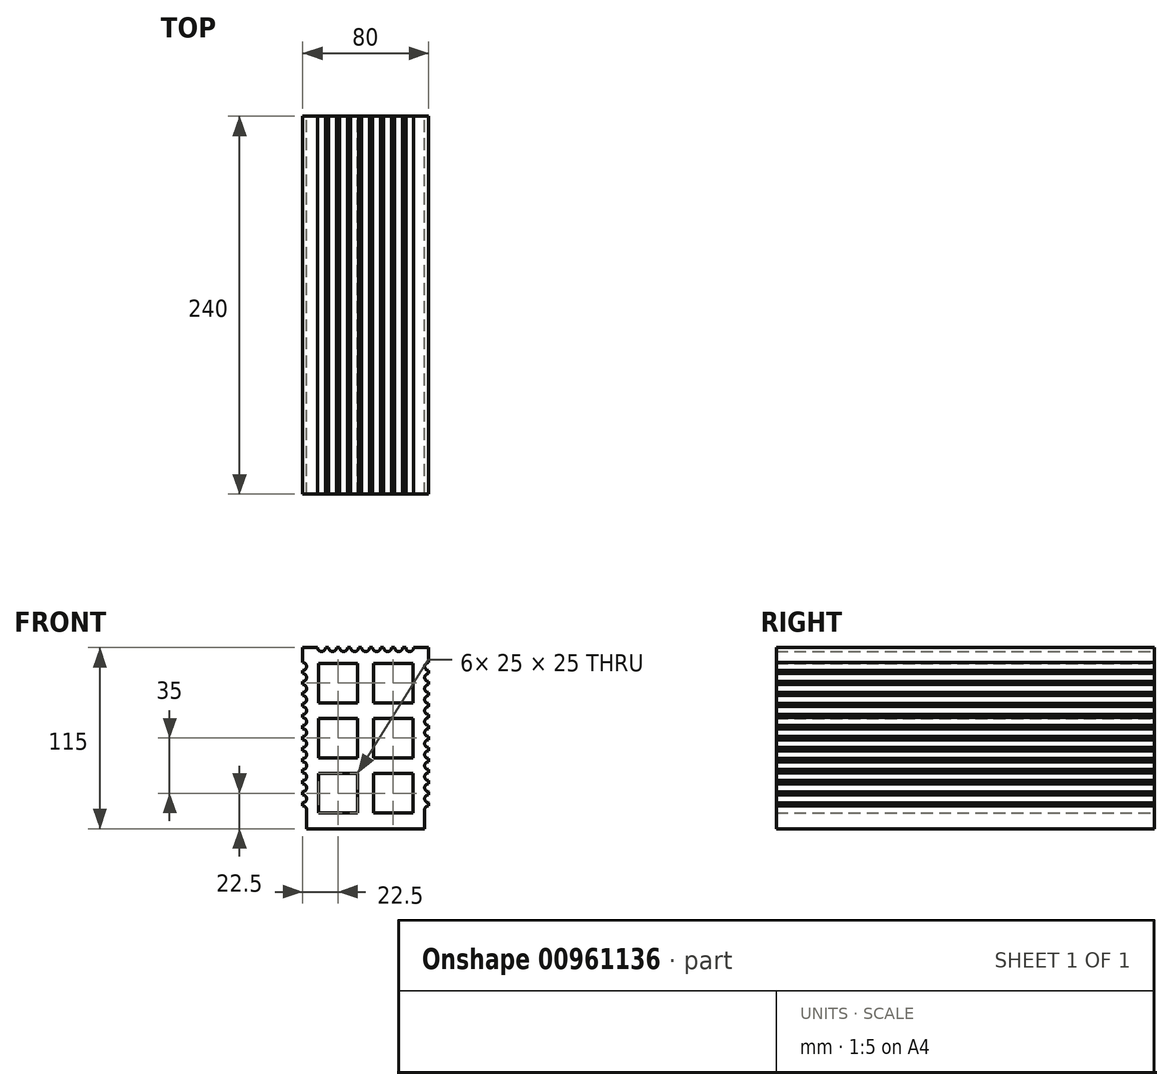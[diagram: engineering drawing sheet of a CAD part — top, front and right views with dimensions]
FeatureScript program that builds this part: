
annotation { "Feature Type Name" : "Feature", "Feature Type Description" : "" }
export const myFeature = defineFeature(function(context is Context, id is Id, definition is map)
    precondition{}
    {
        {
            var Q0;
            Q0=qCreatedBy(makeId("Front.planeOp"),FACE);
            var sketch = newSketch(context, id + "F0", { "sketchPlane" : qUnion([Q0])});
            skLineSegment(sketch, "E0.bottom", {"start": v(-40, -57.5) * mm, "end": v(40, -57.5) * mm});
            skLineSegment(sketch, "E0.top", {"start": v(-40, 57.5) * mm, "end": v(40, 57.5) * mm});
            skLineSegment(sketch, "E0.left", {"start": v(-40, -57.5) * mm, "end": v(-40, 57.5) * mm});
            skLineSegment(sketch, "E0.right", {"start": v(40, -57.5) * mm, "end": v(40, 57.5) * mm});
            skLineSegment(sketch, "E1.bottom", {"start": v(-30, 47.5) * mm, "end": v(-5, 47.5) * mm});
            skLineSegment(sketch, "E1.top", {"start": v(-30, 22.5) * mm, "end": v(-5, 22.5) * mm});
            skLineSegment(sketch, "E1.left", {"start": v(-30, 47.5) * mm, "end": v(-30, 22.5) * mm});
            skLineSegment(sketch, "E1.right", {"start": v(-5, 47.5) * mm, "end": v(-5, 22.5) * mm});
            skLineSegment(sketch, "E2.0.1.0", {"start": v(-30, 12.5) * mm, "end": v(-30, -12.5) * mm});
            skLineSegment(sketch, "E2.0.1.1", {"start": v(-30, 12.5) * mm, "end": v(-5, 12.5) * mm});
            skLineSegment(sketch, "E2.0.1.2", {"start": v(-5, 12.5) * mm, "end": v(-5, -12.5) * mm});
            skLineSegment(sketch, "E2.0.1.3", {"start": v(-30, -12.5) * mm, "end": v(-5, -12.5) * mm});
            skLineSegment(sketch, "E2.0.2.0", {"start": v(-30, -22.5) * mm, "end": v(-30, -47.5) * mm});
            skLineSegment(sketch, "E2.0.2.1", {"start": v(-30, -22.5) * mm, "end": v(-5, -22.5) * mm});
            skLineSegment(sketch, "E2.0.2.2", {"start": v(-5, -22.5) * mm, "end": v(-5, -47.5) * mm});
            skLineSegment(sketch, "E2.0.2.3", {"start": v(-30, -47.5) * mm, "end": v(-5, -47.5) * mm});
            skLineSegment(sketch, "E2.1.0.0", {"start": v(5, 47.5) * mm, "end": v(5, 22.5) * mm});
            skLineSegment(sketch, "E2.1.0.1", {"start": v(5, 47.5) * mm, "end": v(30, 47.5) * mm});
            skLineSegment(sketch, "E2.1.0.2", {"start": v(30, 47.5) * mm, "end": v(30, 22.5) * mm});
            skLineSegment(sketch, "E2.1.0.3", {"start": v(5, 22.5) * mm, "end": v(30, 22.5) * mm});
            skLineSegment(sketch, "E2.1.1.0", {"start": v(5, 12.5) * mm, "end": v(5, -12.5) * mm});
            skLineSegment(sketch, "E2.1.1.1", {"start": v(5, 12.5) * mm, "end": v(30, 12.5) * mm});
            skLineSegment(sketch, "E2.1.1.2", {"start": v(30, 12.5) * mm, "end": v(30, -12.5) * mm});
            skLineSegment(sketch, "E2.1.1.3", {"start": v(5, -12.5) * mm, "end": v(30, -12.5) * mm});
            skLineSegment(sketch, "E2.1.2.0", {"start": v(5, -22.5) * mm, "end": v(5, -47.5) * mm});
            skLineSegment(sketch, "E2.1.2.1", {"start": v(5, -22.5) * mm, "end": v(30, -22.5) * mm});
            skLineSegment(sketch, "E2.1.2.2", {"start": v(30, -22.5) * mm, "end": v(30, -47.5) * mm});
            skLineSegment(sketch, "E2.1.2.3", {"start": v(5, -47.5) * mm, "end": v(30, -47.5) * mm});
            skLineSegment(sketch, "E2.direction1", {"start": v(-30, 22.5) * mm, "end": v(5, 22.5) * mm, "construction": true});
            skLineSegment(sketch, "E2.direction2", {"start": v(-30, 22.5) * mm, "end": v(-30, -12.5) * mm, "construction": true});
            skLineSegment(sketch, "E3", {"start": v(-40, 57.5) * mm, "end": v(-40, 48) * mm});
            skLineSegment(sketch, "E4", {"start": v(-40, 48) * mm, "end": v(-40, 43) * mm});
            skLineSegment(sketch, "E5", {"start": v(-40, 43) * mm, "end": v(-40, 41) * mm});
            skLineSegment(sketch, "E6", {"start": v(-37.5, -45.5) * mm, "end": v(-37.5, -57.5) * mm});
            skLineSegment(sketch, "E7", {"start": v(-40, 57.5) * mm, "end": v(-30.5, 57.5) * mm});
            skLineSegment(sketch, "E8", {"start": v(-30.5, 57.5) * mm, "end": v(-25.5, 57.5) * mm});
            skLineSegment(sketch, "E9", {"start": v(-25.5, 57.5) * mm, "end": v(-23.5, 57.5) * mm});
            skArc(sketch, "E10", {"start": v(-30.5, 57.5) * mm, "mid": v(-28, 55) * mm, "end": v(-25.5, 57.5) * mm});
            skArc(sketch, "E11.1.0.0", {"start": v(-23.5, 57.5) * mm, "mid": v(-21, 55) * mm, "end": v(-18.5, 57.5) * mm});
            skLineSegment(sketch, "E11.1.0.1", {"start": v(-18.5, 57.5) * mm, "end": v(-16.5, 57.5) * mm});
            skArc(sketch, "E11.2.0.0", {"start": v(-16.5, 57.5) * mm, "mid": v(-14, 55) * mm, "end": v(-11.5, 57.5) * mm});
            skLineSegment(sketch, "E11.2.0.1", {"start": v(-11.5, 57.5) * mm, "end": v(-9.5, 57.5) * mm});
            skArc(sketch, "E11.3.0.0", {"start": v(-9.5, 57.5) * mm, "mid": v(-7, 55) * mm, "end": v(-4.5, 57.5) * mm});
            skLineSegment(sketch, "E11.3.0.1", {"start": v(-4.5, 57.5) * mm, "end": v(-2.5, 57.5) * mm});
            skArc(sketch, "E11.4.0.0", {"start": v(-2.5, 57.5) * mm, "mid": v(0, 55) * mm, "end": v(2.5, 57.5) * mm});
            skLineSegment(sketch, "E11.4.0.1", {"start": v(2.5, 57.5) * mm, "end": v(4.5, 57.5) * mm});
            skArc(sketch, "E11.5.0.0", {"start": v(4.5, 57.5) * mm, "mid": v(7, 55) * mm, "end": v(9.5, 57.5) * mm});
            skLineSegment(sketch, "E11.5.0.1", {"start": v(9.5, 57.5) * mm, "end": v(11.5, 57.5) * mm});
            skArc(sketch, "E11.6.0.0", {"start": v(11.5, 57.5) * mm, "mid": v(14, 55) * mm, "end": v(16.5, 57.5) * mm});
            skLineSegment(sketch, "E11.6.0.1", {"start": v(16.5, 57.5) * mm, "end": v(18.5, 57.5) * mm});
            skArc(sketch, "E11.7.0.0", {"start": v(18.5, 57.5) * mm, "mid": v(21, 55) * mm, "end": v(23.5, 57.5) * mm});
            skLineSegment(sketch, "E11.7.0.1", {"start": v(23.5, 57.5) * mm, "end": v(25.5, 57.5) * mm});
            skArc(sketch, "E11.8.0.0", {"start": v(25.5, 57.5) * mm, "mid": v(28, 55) * mm, "end": v(30.5, 57.5) * mm});
            skLineSegment(sketch, "E11.direction1", {"start": v(-30.5, 57.5) * mm, "end": v(-23.5, 57.5) * mm, "construction": true});
            skArc(sketch, "E12", {"start": v(-40, 43) * mm, "mid": v(-37.5, 45.5) * mm, "end": v(-40, 48) * mm});
            skArc(sketch, "E13.0.1.0", {"start": v(-40, 36) * mm, "mid": v(-37.5, 38.5) * mm, "end": v(-40, 41) * mm});
            skArc(sketch, "E13.0.2.0", {"start": v(-40, 29) * mm, "mid": v(-37.5, 31.5) * mm, "end": v(-40, 34) * mm});
            skArc(sketch, "E13.0.3.0", {"start": v(-40, 22) * mm, "mid": v(-37.5, 24.5) * mm, "end": v(-40, 27) * mm});
            skArc(sketch, "E13.0.4.0", {"start": v(-40, 15) * mm, "mid": v(-37.5, 17.5) * mm, "end": v(-40, 20) * mm});
            skArc(sketch, "E13.0.5.0", {"start": v(-40, 8) * mm, "mid": v(-37.5, 10.5) * mm, "end": v(-40, 13) * mm});
            skArc(sketch, "E13.0.6.0", {"start": v(-40, 1) * mm, "mid": v(-37.5, 3.5) * mm, "end": v(-40, 6) * mm});
            skArc(sketch, "E13.0.7.0", {"start": v(-40, -6) * mm, "mid": v(-37.5, -3.5) * mm, "end": v(-40, -1) * mm});
            skArc(sketch, "E13.0.8.0", {"start": v(-40, -13) * mm, "mid": v(-37.5, -10.5) * mm, "end": v(-40, -8) * mm});
            skArc(sketch, "E13.0.9.0", {"start": v(-40, -20) * mm, "mid": v(-37.5, -17.5) * mm, "end": v(-40, -15) * mm});
            skArc(sketch, "E13.0.10.0", {"start": v(-40, -27) * mm, "mid": v(-37.5, -24.5) * mm, "end": v(-40, -22) * mm});
            skArc(sketch, "E13.0.11.0", {"start": v(-40, -34) * mm, "mid": v(-37.5, -31.5) * mm, "end": v(-40, -29) * mm});
            skArc(sketch, "E13.0.12.0", {"start": v(-40, -41) * mm, "mid": v(-37.5, -38.5) * mm, "end": v(-40, -36) * mm});
            skArc(sketch, "E13.0.13.0", {"start": v(-40, -48) * mm, "mid": v(-37.5, -45.5) * mm, "end": v(-40, -43) * mm});
            skLineSegment(sketch, "E13.direction1", {"start": v(-40, 43) * mm, "end": v(-52.04, 43) * mm, "construction": true});
            skLineSegment(sketch, "E13.direction2", {"start": v(-40, 43) * mm, "end": v(-40, 36) * mm, "construction": true});
            skArc(sketch, "E14.MirrorCS", {"start": v(40, 43) * mm, "mid": v(37.5, 45.5) * mm, "end": v(40, 48) * mm});
            skArc(sketch, "E15.MirrorCS", {"start": v(40, 36) * mm, "mid": v(37.5, 38.5) * mm, "end": v(40, 41) * mm});
            skArc(sketch, "E16.MirrorCS", {"start": v(40, 29) * mm, "mid": v(37.5, 31.5) * mm, "end": v(40, 34) * mm});
            skArc(sketch, "E17.MirrorCS", {"start": v(40, 22) * mm, "mid": v(37.5, 24.5) * mm, "end": v(40, 27) * mm});
            skArc(sketch, "E18.MirrorCS", {"start": v(40, 15) * mm, "mid": v(37.5, 17.5) * mm, "end": v(40, 20) * mm});
            skArc(sketch, "E19.MirrorCS", {"start": v(40, 8) * mm, "mid": v(37.5, 10.5) * mm, "end": v(40, 13) * mm});
            skArc(sketch, "E20.MirrorCS", {"start": v(40, 1) * mm, "mid": v(37.5, 3.5) * mm, "end": v(40, 6) * mm});
            skArc(sketch, "E21.MirrorCS", {"start": v(40, -6) * mm, "mid": v(37.5, -3.5) * mm, "end": v(40, -1) * mm});
            skArc(sketch, "E22.MirrorCS", {"start": v(40, -13) * mm, "mid": v(37.5, -10.5) * mm, "end": v(40, -8) * mm});
            skArc(sketch, "E23.MirrorCS", {"start": v(40, -20) * mm, "mid": v(37.5, -17.5) * mm, "end": v(40, -15) * mm});
            skArc(sketch, "E24.MirrorCS", {"start": v(40, -27) * mm, "mid": v(37.5, -24.5) * mm, "end": v(40, -22) * mm});
            skArc(sketch, "E25.MirrorCS", {"start": v(40, -34) * mm, "mid": v(37.5, -31.5) * mm, "end": v(40, -29) * mm});
            skArc(sketch, "E26.MirrorCS", {"start": v(40, -41) * mm, "mid": v(37.5, -38.5) * mm, "end": v(40, -36) * mm});
            skArc(sketch, "E27.MirrorCS", {"start": v(40, -48) * mm, "mid": v(37.5, -45.5) * mm, "end": v(40, -43) * mm});
            skLineSegment(sketch, "E28.MirrorCS", {"start": v(37.5, -45.5) * mm, "end": v(37.5, -57.5) * mm});
            skSolve(sketch);
        }
        {
            var Q0;
            Q0=makeQuery(id+"F0.imprint","IMPRINT",FACE,{"disambiguationData":[TD([[makeQuery(id+"F0.imprint","IMPRINT",EDGE,{"derivedFrom":sQuery(id+"F0.wireOp",EDGE,"E1.bottom")}),1.0]])]});
            extrude(context, id + "F1", {"entities" : qUnion([Q0]), "depth" : 240 * mm, "offsetDistance" : 25 * mm});
        }
    });
